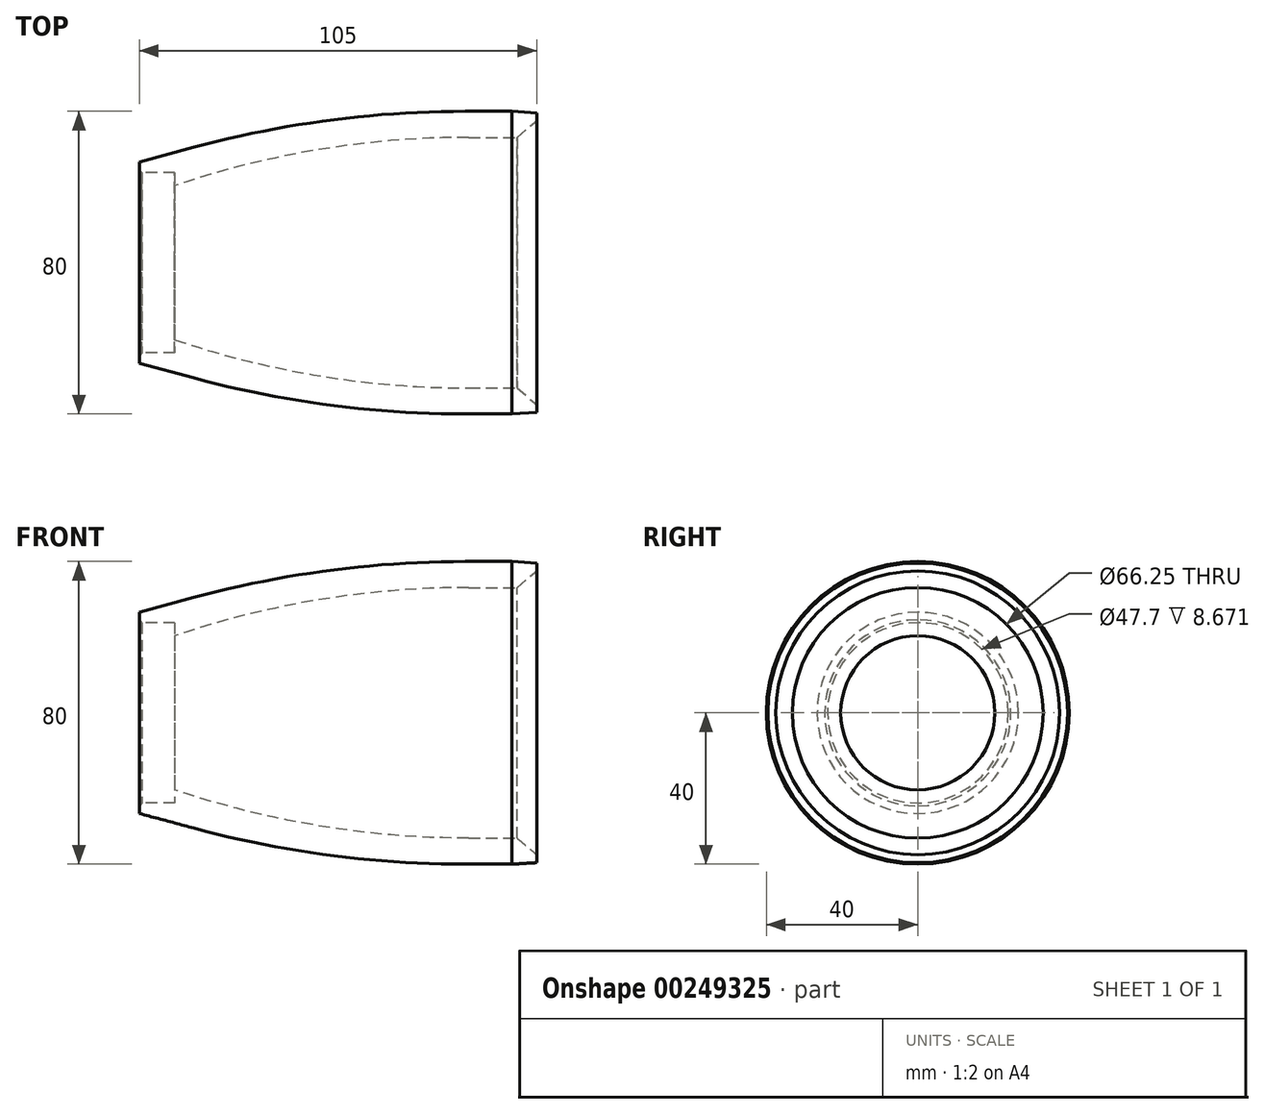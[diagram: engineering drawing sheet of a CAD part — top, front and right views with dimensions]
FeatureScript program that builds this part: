
annotation { "Feature Type Name" : "Feature", "Feature Type Description" : "" }
export const myFeature = defineFeature(function(context is Context, id is Id, definition is map)
    precondition{}
    {
        {
            var Q0;
            Q0=qCreatedBy(makeId("Front.planeOp"),FACE);
            var sketch = newSketch(context, id + "F0", { "sketchPlane" : qUnion([Q0])});
            skLineSegment(sketch, "E0", {"start": v(-5.22, 33.12) * mm, "end": v(-18, 33.12) * mm});
            skLineSegment(sketch, "E1", {"start": v(0, 37.5) * mm, "end": v(0, 39.6) * mm});
            skLineSegment(sketch, "E2", {"start": v(0, 39.6) * mm, "end": v(-6.54, 40) * mm});
            skLineSegment(sketch, "E3", {"start": v(-6.54, 40) * mm, "end": v(-18.91, 40) * mm});
            skLineSegment(sketch, "E4", {"start": v(0, 0) * mm, "end": v(-138.02, 0) * mm});
            skLineSegment(sketch, "E5", {"start": v(-105, 26.6) * mm, "end": v(-90.66, 30.48) * mm});
            skLineSegment(sketch, "E6", {"start": v(-105, 26.6) * mm, "end": v(-105, 24.6) * mm});
            skLineSegment(sketch, "E7", {"start": v(-105, 24.6) * mm, "end": v(-101.14, 20) * mm});
            skLineSegment(sketch, "E8", {"start": v(0, 37.5) * mm, "end": v(-5.22, 33.12) * mm});
            skPoint(sketch, "E9.orphan", {"position": v(0, 33.12) * mm});
            skLineSegment(sketch, "E10", {"start": v(-97.46, 29.14) * mm, "end": v(-105.18, 27.05) * mm, "construction": true});
            skLineSegment(sketch, "E11", {"start": v(-105.18, 27.05) * mm, "end": v(-105, 26.37) * mm, "construction": true});
            skLineSegment(sketch, "E12", {"start": v(-105, 26.37) * mm, "end": v(-97.28, 28.46) * mm, "construction": true});
            skLineSegment(sketch, "E13", {"start": v(-97.46, 29.14) * mm, "end": v(-97.28, 28.46) * mm, "construction": true});
            skLineSegment(sketch, "E14", {"start": v(-101.14, 20) * mm, "end": v(-100.23, 20) * mm});
            skLineSegment(sketch, "E15", {"start": v(-100.23, 20) * mm, "end": v(-98.5, 23) * mm});
            skLineSegment(sketch, "E16", {"start": v(-98.5, 23) * mm, "end": v(-96.77, 20) * mm});
            skPoint(sketch, "E17.visualSharp", {"position": v(-54.5, 33.12) * mm});
            skPoint(sketch, "E18.visualSharp", {"position": v(-55.42, 40) * mm});
            skArc(sketch, "E18.filletArc", {"start": v(-18.91, 40) * mm, "mid": v(-55.1, 37.6) * mm, "end": v(-90.66, 30.48) * mm});
            skArc(sketch, "E19", {"start": v(-18, 33.12) * mm, "mid": v(-57.93, 29.82) * mm, "end": v(-96.77, 20) * mm});
            skSolve(sketch);
        }
        {
            var Q0;
            Q0=makeQuery(id+"F0.imprint","IMPRINT",FACE,{"disambiguationData":[TD([[makeQuery(id+"F0.imprint","IMPRINT",EDGE,{"derivedFrom":sQuery(id+"F0.wireOp",EDGE,"E0")}),-1.0]])]});
            var Q1;
            Q1=sQuery(id+"F0.wireOp",EDGE,"E4");
            revolve(context, id + "F1", {"entities" : qUnion([Q0]), "axis" : qUnion([Q1]), "revolveType" : RevolveType.SYMMETRIC, "angle" : 360 * degree});
        }
        {
            var Q0;
            Q0=makeQuery(id+"F1.opRevolve","SWEPT_FACE",FACE,{"disambiguationData":[OSD([sQuery(id+"F0.wireOp",EDGE,"E6")])]});
            var sketch = newSketch(context, id + "F2", { "sketchPlane" : qUnion([Q0])});
            skCircle(sketch, "E20", {"center": v(0, 0) * mm, "radius": 23.85 * mm});
            skSolve(sketch);
        }
        {
            var Q0;
            Q0=makeQuery(id+"F2.imprint","IMPRINT",FACE,{"disambiguationData":[TD([[makeQuery(id+"F2.imprint","IMPRINT",EDGE,{"derivedFrom":sQuery(id+"F2.wireOp",EDGE,"E20")}),1.0]])]});
            extrude(context, id + "F3", {"entities" : qUnion([Q0]), "operationType" : NewBodyOperationType.REMOVE, "oppositeDirection" : true, "depth" : 9.3 * mm, "offsetDistance" : 25 * mm});
        }
    });
